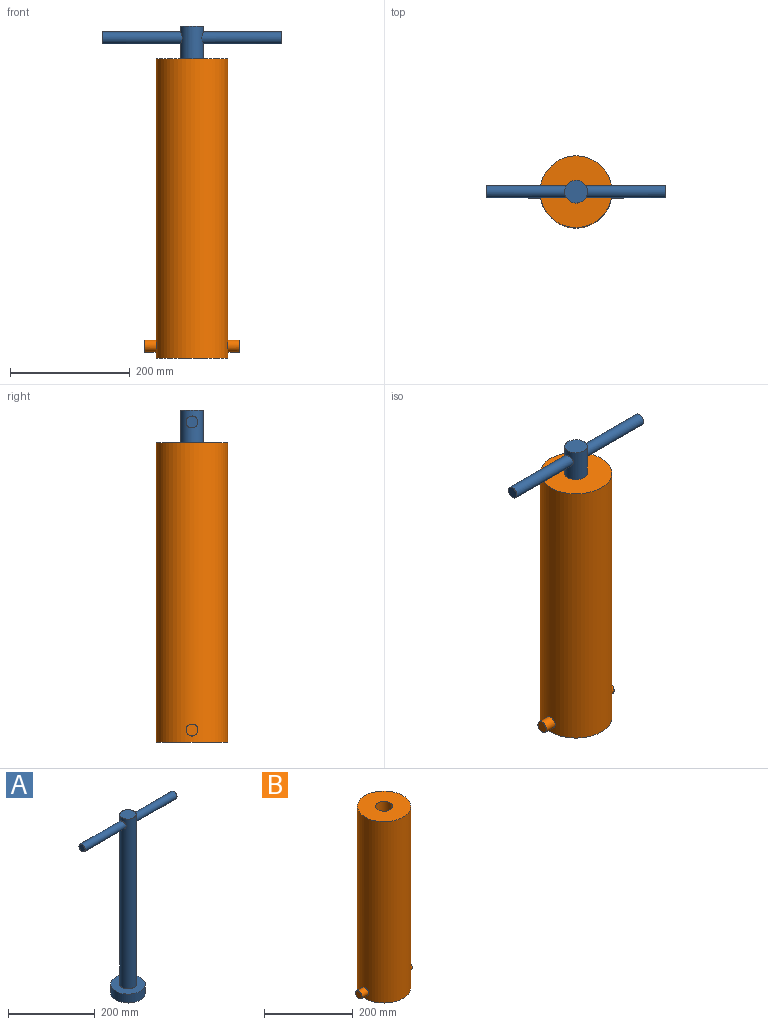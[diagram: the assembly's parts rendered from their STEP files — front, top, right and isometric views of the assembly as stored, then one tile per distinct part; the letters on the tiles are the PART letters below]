
ASSEMBLY  parts=2 mates=1
PART A: 9 faces, bbox 300x80x505 mm
  f0: cylinder r=19mm len=480mm, axis (0,0,-1), area 56649.6mm2, adj f1,f4,f6,f7
  f1: plane 38x38mm, normal (0,0,1), area 1134.1mm2, adj f0
  f2: cylinder r=40mm len=80mm, axis (0,0,1), area 6283.2mm2, adj f3,f4
  f3: plane 80x80mm, normal (0,0,-1), area 5026.5mm2, adj f2
  f4: plane 80x80mm, normal (0,0,1), area 3892.4mm2, adj f0,f2
  f5: plane 20x20mm, normal (1,0,0), area 314.2mm2, adj f6
  f6: cylinder r=10mm len=133.85mm, axis (-1,0,0), area 8318.5mm2, adj f0,f5
  f7: cylinder r=10mm len=133.85mm, axis (-1,0,0), area 8318.6mm2, adj f0,f8
  f8: plane 20x20mm, normal (-1,0,0), area 314.2mm2, adj f7
PART B: 11 faces, bbox 160x120x500 mm
  f0: cylinder r=60mm len=500mm, axis (0,0,-1), area 187863.5mm2, adj f1,f2,f8,f9
  f1: plane 120x120mm, normal (0,0,1), area 10175.6mm2, adj f0,f3
  f2: plane 120x120mm, normal (0,0,-1), area 11309.7mm2, adj f0
  f3: cylinder r=19mm len=38mm, axis (0,0,1), area 3581.4mm2, adj f1,f4
  f4: plane 80x80mm, normal (0,0,-1), area 3892.4mm2, adj f3,f5
  f5: cylinder r=40mm len=430mm, axis (0,0,1), area 108070.8mm2, adj f4,f6
  f6: plane 80x80mm, normal (0,0,1), area 5026.5mm2, adj f5
  f7: plane 20x20mm, normal (1,0,0), area 314.2mm2, adj f8
  f8: cylinder r=10mm len=20.84mm, axis (-1,0,0), area 1283mm2, adj f0,f7
  f9: cylinder r=10mm len=20.84mm, axis (-1,0,0), area 1283mm2, adj f0,f10
  f10: plane 20x20mm, normal (-1,0,0), area 314.2mm2, adj f9
PLACE A t=(0,0,75)mm
PLACE B at identity fixed
MATE slider A.f2 <-> B.f0  axis (0,0,-1) through (0,0,50)mm
